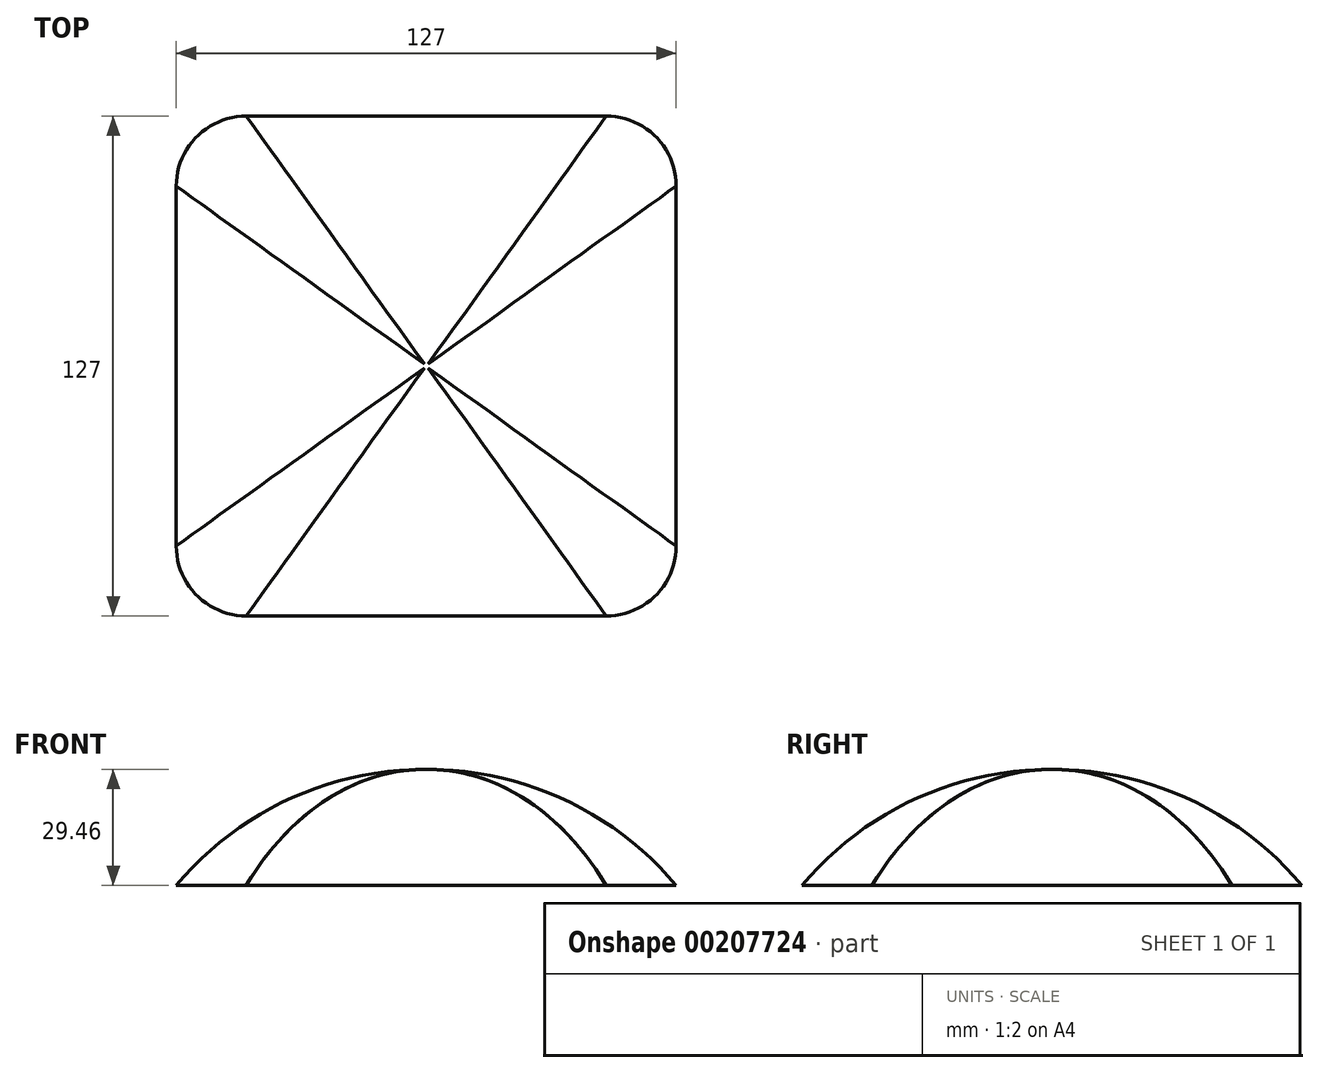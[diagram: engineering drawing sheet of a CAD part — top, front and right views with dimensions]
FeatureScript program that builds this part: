
annotation { "Feature Type Name" : "Feature", "Feature Type Description" : "" }
export const myFeature = defineFeature(function(context is Context, id is Id, definition is map)
    precondition{}
    {
        {
            var Q0;
            Q0=qCreatedBy(makeId("Top.planeOp"),FACE);
            var sketch = newSketch(context, id + "F0", { "sketchPlane" : qUnion([Q0])});
            skLineSegment(sketch, "E0.bottom", {"start": v(-29.94, 84.83) * mm, "end": v(61.5, 84.83) * mm});
            skLineSegment(sketch, "E0.top", {"start": v(-29.94, -42.17) * mm, "end": v(61.5, -42.17) * mm});
            skLineSegment(sketch, "E0.left", {"start": v(-47.72, 67.05) * mm, "end": v(-47.72, -24.39) * mm});
            skLineSegment(sketch, "E0.right", {"start": v(79.28, 67.05) * mm, "end": v(79.28, -24.39) * mm});
            skArc(sketch, "E1.filletArc", {"start": v(-29.94, 84.83) * mm, "mid": v(-42.51, 79.63) * mm, "end": v(-47.72, 67.05) * mm});
            skArc(sketch, "E2.filletArc", {"start": v(79.28, 67.05) * mm, "mid": v(74.07, 79.63) * mm, "end": v(61.5, 84.83) * mm});
            skArc(sketch, "E3.filletArc", {"start": v(61.5, -42.17) * mm, "mid": v(74.07, -36.96) * mm, "end": v(79.28, -24.39) * mm});
            skArc(sketch, "E4.filletArc", {"start": v(-47.72, -24.39) * mm, "mid": v(-42.51, -36.96) * mm, "end": v(-29.94, -42.17) * mm});
            skSolve(sketch);
        }
        {
            var Q0;
            Q0=makeQuery(id+"F0.imprint","IMPRINT",FACE,{"disambiguationData":[TD([[makeQuery(id+"F0.imprint","IMPRINT",EDGE,{"derivedFrom":sQuery(id+"F0.wireOp",EDGE,"E0.bottom")}),-1.0]])]});
            extrude(context, id + "F1", {"entities" : qUnion([Q0]), "depth" : 29.46 * mm});
        }
        {
            var Q0;
            Q0=makeQuery(id+"F1.opExtrude","CAP_EDGE",EDGE,{"disambiguationData":[OSD([sQuery(id+"F0.wireOp",EDGE,"E0.bottom")])],"isStart":false});
            fillet(context, id + "F2", {"entities" : qUnion([Q0]), "radius" : 82.17 * mm, "tangentPropagation" : true, "allowEdgeOverflow" : false});
        }
        {
            var Q0;
            Q0=makeQuery(id+"F1.opExtrude","SWEPT_BODY",BODY,{"disambiguationData":[OSD([sQuery(id+"F0.wireOp",EDGE,"E0.bottom"),sQuery(id+"F0.wireOp",EDGE,"E0.top"),sQuery(id+"F0.wireOp",EDGE,"E0.left"),sQuery(id+"F0.wireOp",EDGE,"E0.right"),sQuery(id+"F0.wireOp",EDGE,"E1.filletArc"),sQuery(id+"F0.wireOp",EDGE,"E2.filletArc"),sQuery(id+"F0.wireOp",EDGE,"E3.filletArc"),sQuery(id+"F0.wireOp",EDGE,"E4.filletArc")])]});
            var Q1;
            {var subQ0=sQuery(id+"F0.wireOp",EDGE,"E0.left");Q1=makeQuery(id+"F2.opFillet","BLEND_EDGE",EDGE,{"disambiguationData":[OD(1.0)],"blendedFrom":[makeQuery(id+"F1.opExtrude","CAP_EDGE",EDGE,{"disambiguationData":[OSD([subQ0])],"isStart":false}),makeQuery(id+"F1.opExtrude","CAP_FACE",FACE,{"disambiguationData":[OSD([sQuery(id+"F0.wireOp",EDGE,"E0.bottom"),sQuery(id+"F0.wireOp",EDGE,"E0.top"),subQ0,sQuery(id+"F0.wireOp",EDGE,"E0.right"),sQuery(id+"F0.wireOp",EDGE,"E1.filletArc"),sQuery(id+"F0.wireOp",EDGE,"E2.filletArc"),sQuery(id+"F0.wireOp",EDGE,"E3.filletArc"),sQuery(id+"F0.wireOp",EDGE,"E4.filletArc")])],"isStart":true})],"blendedInto":[makeQuery(id+"F1.opExtrude","CAP_FACE",FACE,{"disambiguationData":[OSD([sQuery(id+"F0.wireOp",EDGE,"E0.bottom"),sQuery(id+"F0.wireOp",EDGE,"E0.top"),subQ0,sQuery(id+"F0.wireOp",EDGE,"E0.right"),sQuery(id+"F0.wireOp",EDGE,"E1.filletArc"),sQuery(id+"F0.wireOp",EDGE,"E2.filletArc"),sQuery(id+"F0.wireOp",EDGE,"E3.filletArc"),sQuery(id+"F0.wireOp",EDGE,"E4.filletArc")])],"isStart":true})]});}
            transform(context, id + "F3", {"entities" : qUnion([Q0]), "transformType" : TransformType.TRANSLATION_DISTANCE, "transformDirection" : qUnion([Q1]), "distance" : 57.4 * mm, "makeCopy" : false});
        }
    });
